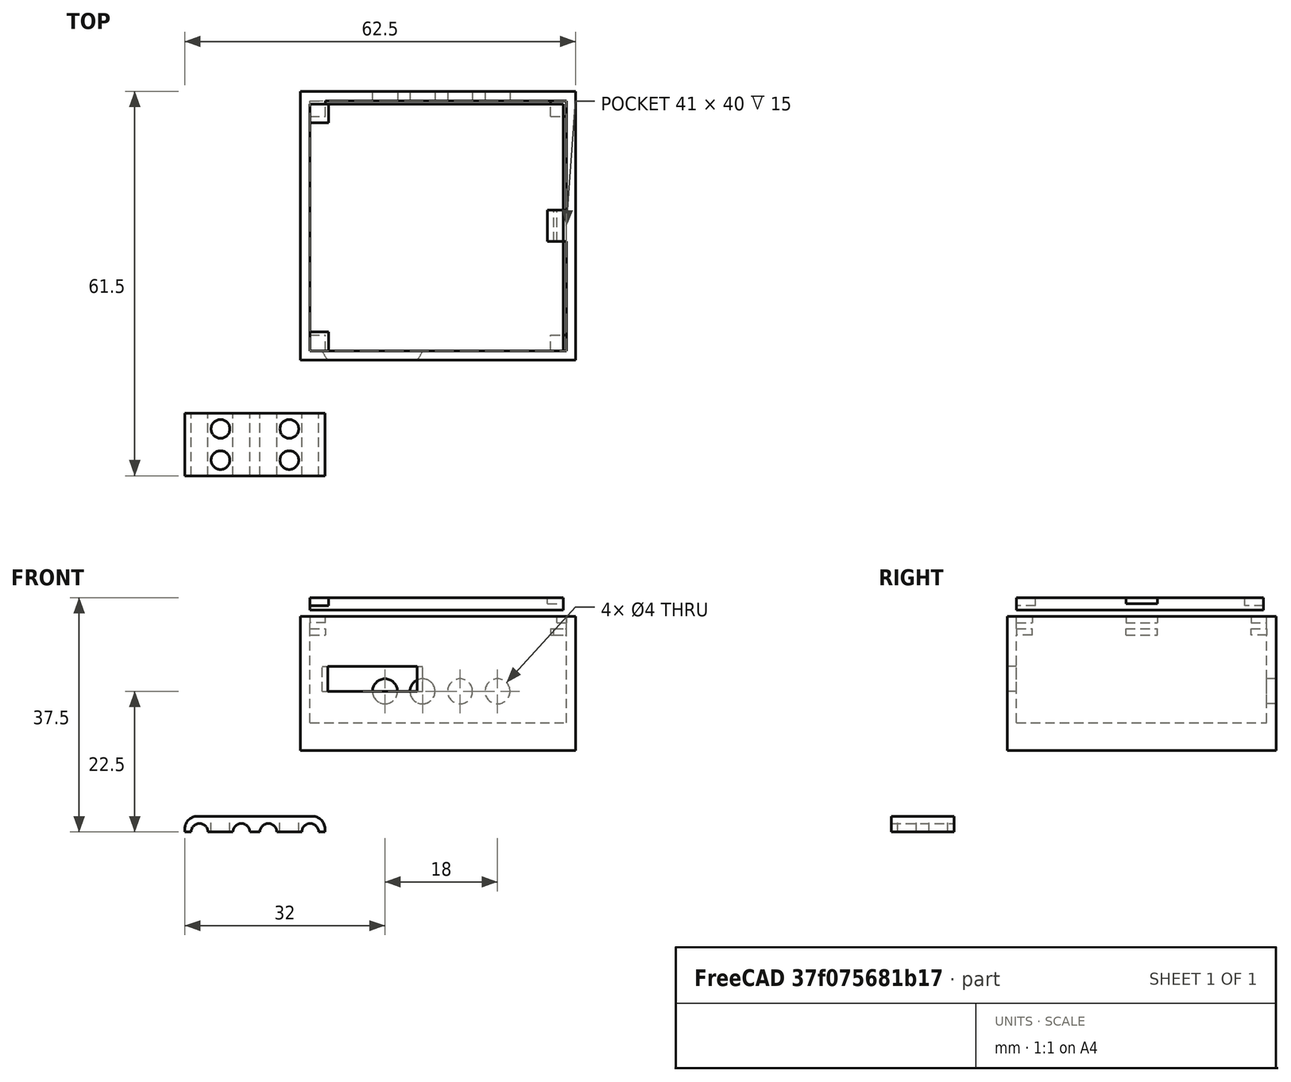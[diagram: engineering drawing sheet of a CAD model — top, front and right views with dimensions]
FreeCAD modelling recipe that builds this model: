
FCSTD DOCUMENT  (FreeCAD 0.17R13522 (Git))
Label: YinXiangTiaoJie-jwei-1.0
License: All rights reserved
LicenseURL: http://en.wikipedia.org/wiki/All_rights_reserved
objects: Part::Box×18, Part::Cylinder×13, Part::MultiFuse×12, Part::Cut×7, Part::Fillet×1
note: 51 computed .brp shape members not serialized (recipe doc carries the construction recipe); baked Part::Feature solids carry a one-line shape summary decoded from their .brp

FEATURE [Part::Box] Box  label="立方体"
  AttacherType = Attacher::AttachEngine3D
  Height = 15
  Length = 41
  Placement = pos=(20,20,20) rot=(0,0,1;0rad)
  Width = 40
FEATURE [Part::Cylinder] Cylinder  label="圆柱体"
  Angle = 360
  AttacherType = Attacher::AttachEngine3D
  Height = 4
  Placement = pos=(30,24,25) rot=(0,0,1;0rad)
  Radius = 9
FEATURE [Part::MultiFuse] Fusion  label="主"
  Shapes = -> [Box,Cylinder]
FEATURE [Part::Box] Box001  label="立方体001"
  AttacherType = Attacher::AttachEngine3D
  Height = 19.5
  Length = 44
  Placement = pos=(18.5,18.5,15.5) rot=(0,0,1;0rad)
  Width = 43
FEATURE [Part::Box] Box002  label="立方体002"
  AttacherType = Attacher::AttachEngine3D
  Height = 2
  Length = 40.5
  Placement = pos=(20,20,31) rot=(0,0,1;0rad)
  Width = 39.5
FEATURE [Part::Box] Box003  label="立方体003"
  AttacherType = Attacher::AttachEngine3D
  Height = 1
  Length = 4
  Placement = pos=(18.5,18.5,30) rot=(0,0,1;0rad)
  Width = 4
FEATURE [Part::Box] Box004  label="立方体004"
  AttacherType = Attacher::AttachEngine3D
  Height = 1
  Length = 4
  Placement = pos=(18.5,57.5,30) rot=(0,0,1;0rad)
  Width = 4
FEATURE [Part::Box] Box005  label="立方体005"
  AttacherType = Attacher::AttachEngine3D
  Height = 1.3
  Length = 4.5
  Placement = pos=(18.5,18.5,31.7) rot=(0,0,1;0rad)
  Width = 4.5
FEATURE [Part::Box] Box006  label="立方体006"
  AttacherType = Attacher::AttachEngine3D
  Height = 1.3
  Length = 4.5
  Placement = pos=(18.5,56.5,31.7) rot=(0,0,1;0rad)
  Width = 4.5
FEATURE [Part::Box] Box007  label="立方体007"
  AttacherType = Attacher::AttachEngine3D
  Height = 1
  Length = 2.5
  Placement = pos=(58,37.5,32) rot=(0,0,1;0rad)
  Width = 5
FEATURE [Part::Box] Box008  label="立方体008"
  AttacherType = Attacher::AttachEngine3D
  Height = 1
  Length = 2
  Placement = pos=(59,37.5,30) rot=(0,0,1;0rad)
  Width = 5
FEATURE [Part::MultiFuse] Fusion001
  Shapes = -> [Box006,Box005,Box007]
FEATURE [Part::Cut] Cut  label="盖"
  Base = -> Box002
  Placement = pos=(0,0,7) rot=(0,0,1;0rad)
  Tool = -> Fusion001
FEATURE [Part::Box] Box009  label="立方体009"
  AttacherType = Attacher::AttachEngine3D
  Height = 1
  Length = 2
  Placement = pos=(59.5,37.5,32) rot=(0,0,1;0rad)
  Width = 5
FEATURE [Part::Box] Box010  label="立方体010"
  AttacherType = Attacher::AttachEngine3D
  Height = 1
  Length = 4
  Placement = pos=(18.5,57.5,32) rot=(0,0,1;0rad)
  Width = 4
FEATURE [Part::Box] Box011  label="立方体011"
  AttacherType = Attacher::AttachEngine3D
  Height = 1
  Length = 4
  Placement = pos=(18.5,18.5,32) rot=(0,0,1;0rad)
  Width = 4
FEATURE [Part::Cut] Cut001
  Base = -> Box001
  Tool = -> Fusion
FEATURE [Part::MultiFuse] Fusion002
  Placement = pos=(0,0,4) rot=(0,0,1;0rad)
  Shapes = -> [Box008,Box004,Box003]
FEATURE [Part::MultiFuse] Fusion003
  Shapes = -> [Cut001,Fusion002]
FEATURE [Part::Box] Box012  label="立方体012"
  AttacherType = Attacher::AttachEngine3D
  Height = 2
  Length = 44
  Placement = pos=(18.5,18.5,32) rot=(0,0,1;0rad)
  Width = 43
FEATURE [Part::MultiFuse] Fusion004
  Placement = pos=(0,0,1) rot=(0,0,1;0rad)
  Shapes = -> [Box011,Box010,Box009]
FEATURE [Part::Box] Box013  label="立方体013"
  AttacherType = Attacher::AttachEngine3D
  Height = 2
  Length = 41
  Placement = pos=(20,20,32) rot=(0,0,1;0rad)
  Width = 40
FEATURE [Part::Cut] Cut002
  Base = -> Box012
  Tool = -> Box013
FEATURE [Part::MultiFuse] Fusion005
  Placement = pos=(0,0,3) rot=(0,0,1;0rad)
  Shapes = -> [Fusion004,Cut002]
FEATURE [Part::MultiFuse] Fusion006  label="aa"
  Shapes = -> [Fusion003,Fusion005]
FEATURE [Part::Cylinder] Cylinder001  label="圆柱体001"
  Angle = 360
  AttacherType = Attacher::AttachEngine3D
  Height = 5
  Placement = pos=(0,6,0) rot=(0,1,0;1.5708rad)
  Radius = 2
FEATURE [Part::Cylinder] Cylinder002  label="圆柱体002"
  Angle = 360
  AttacherType = Attacher::AttachEngine3D
  Height = 5
  Placement = pos=(0,12,0) rot=(0,1,0;1.5708rad)
  Radius = 2
FEATURE [Part::Cylinder] Cylinder003  label="圆柱体003"
  Angle = 360
  AttacherType = Attacher::AttachEngine3D
  Height = 5
  Placement = pos=(0,18,0) rot=(0,1,0;1.5708rad)
  Radius = 2
FEATURE [Part::Cylinder] Cylinder004  label="圆柱体004"
  Angle = 360
  AttacherType = Attacher::AttachEngine3D
  Height = 5
  Placement = pos=(0,0,0) rot=(0,1,0;1.5708rad)
  Radius = 2
FEATURE [Part::MultiFuse] Fusion007
  Placement = pos=(32,63,25) rot=(0,0,-1;1.5708rad)
  Shapes = -> [Cylinder004,Cylinder003,Cylinder002,Cylinder001]
FEATURE [Part::Cut] Cut003  label="aa1"
  Base = -> Fusion006
  Tool = -> Fusion007
FEATURE [Part::Box] Box014  label="立方体014"
  AttacherType = Attacher::AttachEngine3D
  Height = 1
  Length = 4
  Placement = pos=(58.5,57.5,30) rot=(0,0,1;0rad)
  Width = 4
FEATURE [Part::Box] Box015  label="立方体015"
  AttacherType = Attacher::AttachEngine3D
  Height = 1
  Length = 4
  Placement = pos=(58.5,18.5,30) rot=(0,0,1;0rad)
  Width = 4
FEATURE [Part::MultiFuse] Fusion008
  Placement = pos=(0,0,4) rot=(0,0,1;0rad)
  Shapes = -> [Box014,Box015]
FEATURE [Part::MultiFuse] Fusion009  label="壳"
  Shapes = -> [Cut003,Fusion008]
FEATURE [Part::Box] Box016  label="立方体016"
  AttacherType = Attacher::AttachEngine3D
  Height = 5
  Length = 22.4
  Width = 10
FEATURE [Part::Cylinder] Cylinder005  label="圆柱体005"
  Angle = 360
  AttacherType = Attacher::AttachEngine3D
  Height = 10
  Placement = pos=(2.35,0,2.5) rot=(1,0,0;4.71239rad)
  Radius = 1.35
FEATURE [Part::Cylinder] Cylinder006  label="圆柱体006"
  Angle = 360
  AttacherType = Attacher::AttachEngine3D
  Height = 10
  Placement = pos=(9.05,0,2.5) rot=(-1,0,0;1.5708rad)
  Radius = 1.35
FEATURE [Part::Cylinder] Cylinder007  label="圆柱体007"
  Angle = 360
  AttacherType = Attacher::AttachEngine3D
  Height = 10
  Placement = pos=(13.35,0,2.5) rot=(-1,0,0;1.5708rad)
  Radius = 1.35
FEATURE [Part::Cylinder] Cylinder008  label="圆柱体008"
  Angle = 360
  AttacherType = Attacher::AttachEngine3D
  Height = 10
  Placement = pos=(20.05,0,2.5) rot=(-1,0,0;1.5708rad)
  Radius = 1.35
FEATURE [Part::MultiFuse] Fusion010
  Shapes = -> [Cylinder008,Cylinder007,Cylinder006,Cylinder005]
FEATURE [Part::Cut] Cut004
  Base = -> Box016
  Tool = -> Fusion010
FEATURE [Part::Box] Box017  label="立方体017"
  AttacherType = Attacher::AttachEngine3D
  Height = 2.5
  Length = 22.4
  Width = 10
FEATURE [Part::Cut] Cut005
  Base = -> Cut004
  Tool = -> Box017
FEATURE [Part::Cylinder] Cylinder009  label="圆柱体009"
  Angle = 360
  AttacherType = Attacher::AttachEngine3D
  Height = 5
  Placement = pos=(5.7,2.5,0) rot=(0,0,1;0rad)
  Radius = 1.5
FEATURE [Part::Cylinder] Cylinder010  label="圆柱体010"
  Angle = 360
  AttacherType = Attacher::AttachEngine3D
  Height = 5
  Placement = pos=(5.7,7.5,0) rot=(0,0,1;0rad)
  Radius = 1.5
FEATURE [Part::Cylinder] Cylinder011  label="圆柱体011"
  Angle = 360
  AttacherType = Attacher::AttachEngine3D
  Height = 5
  Placement = pos=(16.7,2.5,0) rot=(0,0,1;0rad)
  Radius = 1.5
FEATURE [Part::Cylinder] Cylinder012  label="圆柱体012"
  Angle = 360
  AttacherType = Attacher::AttachEngine3D
  Height = 5
  Placement = pos=(16.7,7.5,0) rot=(0,0,1;0rad)
  Radius = 1.5
FEATURE [Part::MultiFuse] Fusion011
  Shapes = -> [Cylinder012,Cylinder011,Cylinder010,Cylinder009]
FEATURE [Part::Cut] Cut006
  Base = -> Cut005
  Tool = -> Fusion011
FEATURE [Part::Fillet] Fillet  label="线卡"
  Base = -> Cut006
  Edges = 2 edges r=2: [Edge2,Edge17]
